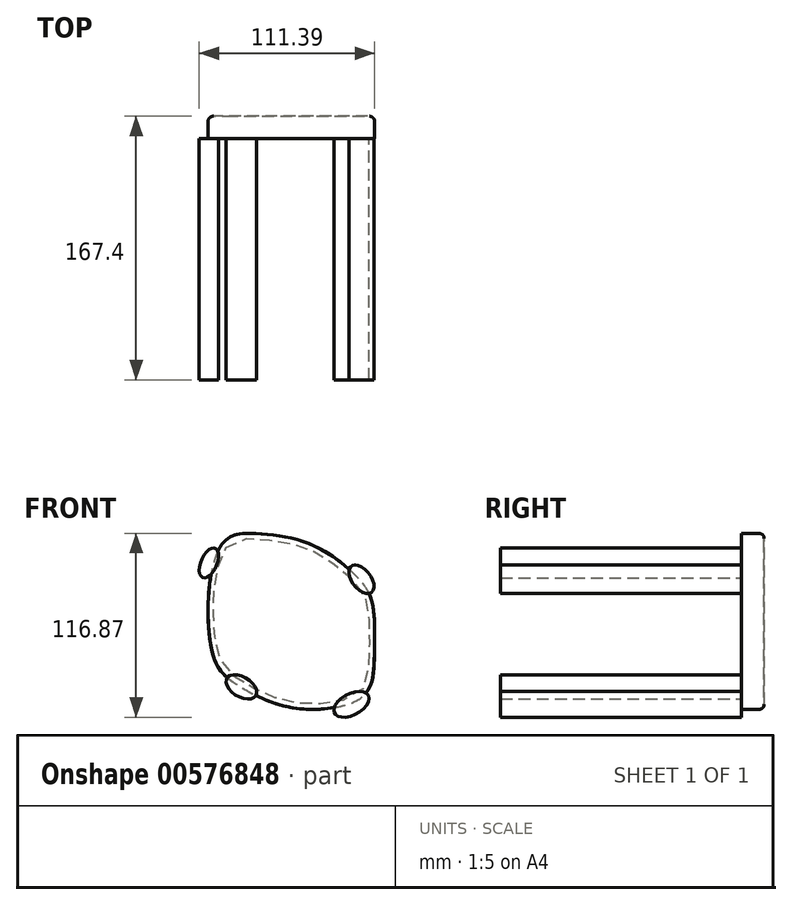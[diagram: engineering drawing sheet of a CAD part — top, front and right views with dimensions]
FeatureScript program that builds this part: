
annotation { "Feature Type Name" : "Feature", "Feature Type Description" : "" }
export const myFeature = defineFeature(function(context is Context, id is Id, definition is map)
    precondition{}
    {
        {
            var Q0;
            Q0=qCreatedBy(makeId("Top.planeOp"),FACE);
            var sketch = newSketch(context, id + "F0", { "sketchPlane" : qUnion([Q0])});
            skEllipse(sketch, "E0", {"center": v(55.6, 0) * mm, "majorRadius": 10.7 * mm, "minorRadius": 6.29 * mm, "majorAxis": v(1, 0)});
            skSolve(sketch);
        }
        {
            var Q0;
            Q0=qCreatedBy(makeId("Front.planeOp"),FACE);
            var sketch = newSketch(context, id + "F1", { "sketchPlane" : qUnion([Q0])});
            skFitSpline(sketch, "E1", {"points": [v(56.1, 0) * mm, v(48.4, -30.32) * mm, v(-33.88, -17.55) * mm, v(-38.3, 69.01) * mm, v(45.06, 50.44) * mm, v(56.1, 0) * mm]});
            skSolve(sketch);
        }
        {
            var Q0;
            Q0=qCreatedBy(makeId("Front.planeOp"),FACE);
            var sketch = newSketch(context, id + "F2", { "sketchPlane" : qUnion([Q0])});
            skEllipse(sketch, "E2", {"center": v(-48.44, 56.66) * mm, "majorRadius": 10.1 * mm, "minorRadius": 5.11 * mm, "majorAxis": v(-0.4, -0.92)});
            skSolve(sketch);
        }
        {
            var Q0;
            Q0=qCreatedBy(makeId("Front.planeOp"),FACE);
            var sketch = newSketch(context, id + "F3", { "sketchPlane" : qUnion([Q0])});
            skEllipse(sketch, "E3", {"center": v(48.38, 46.3) * mm, "majorRadius": 10.56 * mm, "minorRadius": 6.02 * mm, "majorAxis": v(0.61, -0.8)});
            skSolve(sketch);
        }
        {
            var Q0;
            Q0=qCreatedBy(makeId("Front.planeOp"),FACE);
            var sketch = newSketch(context, id + "F4", { "sketchPlane" : qUnion([Q0])});
            skEllipse(sketch, "E4", {"center": v(42.06, -33.22) * mm, "majorRadius": 12.13 * mm, "minorRadius": 6.73 * mm, "majorAxis": v(0.89, 0.46)});
            skSolve(sketch);
        }
        {
            var Q0;
            Q0=qCreatedBy(makeId("Front.planeOp"),FACE);
            var sketch = newSketch(context, id + "F5", { "sketchPlane" : qUnion([Q0])});
            skEllipse(sketch, "E5", {"center": v(-27.8, -22.08) * mm, "majorRadius": 10.74 * mm, "minorRadius": 6.32 * mm, "majorAxis": v(0.86, -0.52)});
            skSolve(sketch);
        }
        {
            var Q0;
            Q0 = qSketchRegion(id + "F5", true);
            var Q1;
            Q1 = qSketchRegion(id + "F4", true);
            var Q2;
            Q2 = qSketchRegion(id + "F3", true);
            var Q3;
            Q3 = qSketchRegion(id + "F2", true);
            var Q4;
            Q4=sQuery(id+"F5.wireOp",EDGE,"E5");
            var Q5;
            Q5=sQuery(id+"F2.wireOp",EDGE,"E2");
            var Q6;
            Q6=sQuery(id+"F3.wireOp",EDGE,"E3");
            var Q7;
            Q7=sQuery(id+"F4.wireOp",EDGE,"E4");
            extrude(context, id + "F6", {"entities" : qUnion([Q0, Q1, Q2, Q3]), "surfaceEntities" : qUnion([Q4, Q5, Q6, Q7]), "depth" : 153.1 * mm, "offsetDistance" : 25.4 * mm});
        }
        {
            var Q0;
            Q0=qCreatedBy(makeId("Front.planeOp"),FACE);
            var sketch = newSketch(context, id + "F7", { "sketchPlane" : qUnion([Q0])});
            skFitSpline(sketch, "E6", {"points": [v(-40.31, 68.3) * mm, v(-46.33, 0) * mm, v(-31.8, -19.88) * mm, v(0, -34.42) * mm, v(33.98, -34.66) * mm, v(52.44, -24.54) * mm, v(56.64, 0) * mm, v(56, 27.37) * mm, v(49.07, 43.8) * mm, v(17.6, 67.9) * mm, v(-15.95, 75.08) * mm, v(-40.31, 68.3) * mm]});
            skSolve(sketch);
        }
        {
            var Q0;
            Q0 = qSketchRegion(id + "F7", true);
            extrude(context, id + "F8", {"entities" : qUnion([Q0]), "oppositeDirection" : true, "depth" : 14.3 * mm, "offsetDistance" : 25.4 * mm});
        }
        {
            var Q0;
            Q0=makeQuery(id+"F8.opExtrude","CAP_EDGE",EDGE,{"disambiguationData":[OSD([sQuery(id+"F7.wireOp",EDGE,"E6")])],"isStart":false});
            fillet(context, id + "F9", {"entities" : qUnion([Q0]), "radius" : 3.35 * mm, "tangentPropagation" : true, "allowEdgeOverflow" : false});
        }
    });
